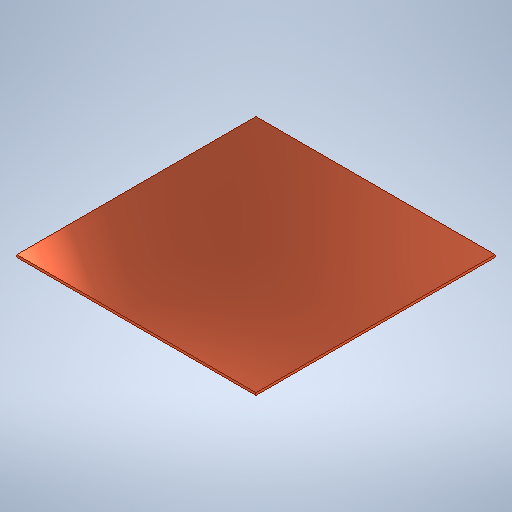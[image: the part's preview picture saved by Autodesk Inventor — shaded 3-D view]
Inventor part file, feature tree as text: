
AUTODESK INVENTOR PART (.ipt)
format: ipt  version: 2025.2 (Build 292293000, 293)  size: 212,992 bytes
history: native  units: mm
features: extrude x1
ambient origin geometry x8: Origin, YZ Plane, XZ Plane, XY Plane, X Axis, Y Axis, Z Axis, Center Point
bodies: Solid1 (feature_tree)
feature tree (1):
  extrude  "Extrusion1"  Depth=100.0mm
